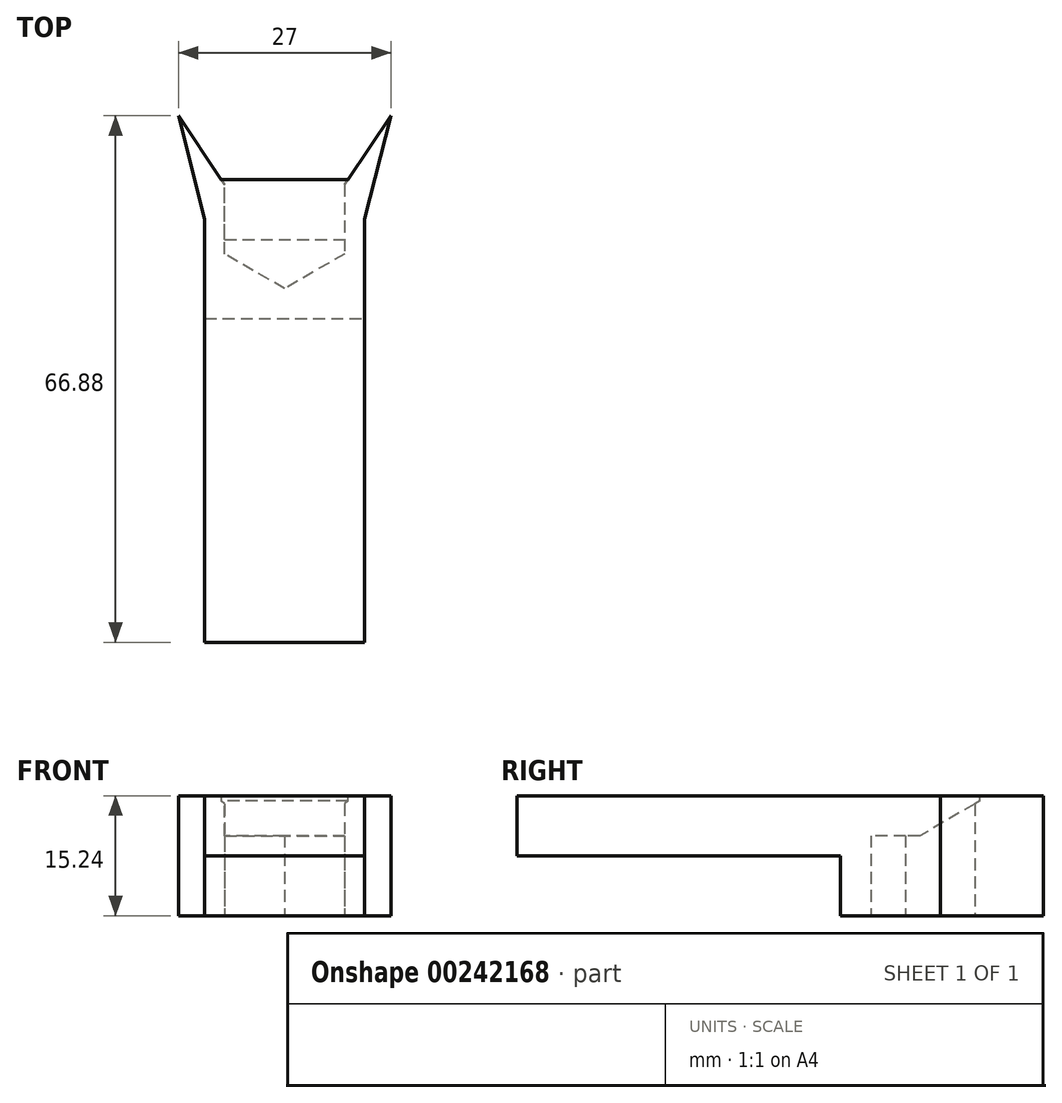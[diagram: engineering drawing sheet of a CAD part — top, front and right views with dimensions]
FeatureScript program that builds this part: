
annotation { "Feature Type Name" : "Feature", "Feature Type Description" : "" }
export const myFeature = defineFeature(function(context is Context, id is Id, definition is map)
    precondition{}
    {
        {
            var Q0;
            Q0=qCreatedBy(makeId("Top.planeOp"),FACE);
            var sketch = newSketch(context, id + "F0", { "sketchPlane" : qUnion([Q0])});
            skLineSegment(sketch, "E0.bottom", {"start": v(-10.19, 14.8) * mm, "end": v(-7.65, 14.8) * mm});
            skLineSegment(sketch, "E0.top", {"start": v(-10.19, -38.95) * mm, "end": v(10.13, -38.95) * mm});
            skLineSegment(sketch, "E0.left", {"start": v(-10.19, 14.8) * mm, "end": v(-10.19, -38.95) * mm});
            skLineSegment(sketch, "E0.right", {"start": v(10.13, 14.8) * mm, "end": v(10.13, -38.95) * mm});
            skArc(sketch, "E1.cCircle", {"start": v(-7.65, 14.8) * mm, "mid": v(-0.03, 7.17) * mm, "end": v(7.6, 14.8) * mm, "construction": true});
            skLineSegment(sketch, "E1.0", {"start": v(7.6, 19.2) * mm, "end": v(7.6, 10.4) * mm});
            skLineSegment(sketch, "E1.1", {"start": v(7.6, 10.4) * mm, "end": v(-0.03, 6) * mm});
            skLineSegment(sketch, "E1.2", {"start": v(-0.03, 6) * mm, "end": v(-7.65, 10.4) * mm});
            skLineSegment(sketch, "E1.3", {"start": v(-7.65, 10.4) * mm, "end": v(-7.65, 19.2) * mm});
            skPoint(sketch, "E1.0.midPoint", {"position": v(7.6, 14.8) * mm});
            skLineSegment(sketch, "E2", {"start": v(-13.5, 27.93) * mm, "end": v(-10.19, 14.8) * mm});
            skLineSegment(sketch, "E3", {"start": v(10.13, 14.8) * mm, "end": v(13.5, 27.93) * mm});
            skLineSegment(sketch, "E4", {"start": v(-13.5, 27.93) * mm, "end": v(-7.65, 19.2) * mm});
            skLineSegment(sketch, "E5", {"start": v(7.6, 19.2) * mm, "end": v(13.5, 27.93) * mm});
            skPoint(sketch, "E6.orphan", {"position": v(-0.03, 23.6) * mm});
            skLineSegment(sketch, "E7.trimOffspring", {"start": v(7.6, 14.8) * mm, "end": v(10.13, 14.8) * mm});
            skSolve(sketch);
        }
        {
            var Q0;
            Q0 = qSketchRegion(id + "F0", true);
            extrude(context, id + "F1", {"entities" : qUnion([Q0]), "depth" : 15.24 * mm});
        }
        {
            var Q0;
            Q0=makeQuery(id+"F1.opExtrude","CAP_FACE",FACE,{"disambiguationData":[OSD([sQuery(id+"F0.wireOp",EDGE,"E0.top"),sQuery(id+"F0.wireOp",EDGE,"E0.left"),sQuery(id+"F0.wireOp",EDGE,"E0.right"),sQuery(id+"F0.wireOp",EDGE,"E1.0"),sQuery(id+"F0.wireOp",EDGE,"E1.1"),sQuery(id+"F0.wireOp",EDGE,"E1.2"),sQuery(id+"F0.wireOp",EDGE,"E1.3"),sQuery(id+"F0.wireOp",EDGE,"E2"),sQuery(id+"F0.wireOp",EDGE,"E3"),sQuery(id+"F0.wireOp",EDGE,"E4"),sQuery(id+"F0.wireOp",EDGE,"E5")])],"isStart":false});
            var sketch = newSketch(context, id + "F2", { "sketchPlane" : qUnion([Q0])});
            skLineSegment(sketch, "E8.bottom", {"start": v(-9.78, 19.84) * mm, "end": v(9.46, 19.84) * mm});
            skLineSegment(sketch, "E8.top", {"start": v(-9.78, 4.74) * mm, "end": v(9.46, 4.74) * mm});
            skLineSegment(sketch, "E8.left", {"start": v(-9.78, 19.84) * mm, "end": v(-9.78, 4.74) * mm});
            skLineSegment(sketch, "E8.right", {"start": v(9.46, 19.84) * mm, "end": v(9.46, 4.74) * mm});
            skSolve(sketch);
        }
        {
            var Q0;
            Q0 = qSketchRegion(id + "F2", true);
            extrude(context, id + "F3", {"entities" : qUnion([Q0]), "operationType" : NewBodyOperationType.ADD, "oppositeDirection" : true, "depth" : 5.08 * mm});
        }
        {
            var Q0;
            Q0=makeQuery(id+"F3.opExtrude","CAP_EDGE",EDGE,{"disambiguationData":[OSD([sQuery(id+"F2.wireOp",EDGE,"E8.bottom")])],"isStart":false});
            chamfer(context, id + "F4", {"entities" : qUnion([Q0]), "chamferType" : ChamferType.OFFSET_ANGLE, "width" : 7.62 * mm, "oppositeDirection" : false, "angle" : 30 * degree, "tangentPropagation" : true});
        }
        {
            var Q0;
            Q0=makeQuery(id+"F1.opExtrude","CAP_FACE",FACE,{"disambiguationData":[OSD([sQuery(id+"F0.wireOp",EDGE,"E0.top"),sQuery(id+"F0.wireOp",EDGE,"E0.left"),sQuery(id+"F0.wireOp",EDGE,"E0.right"),sQuery(id+"F0.wireOp",EDGE,"E1.0"),sQuery(id+"F0.wireOp",EDGE,"E1.1"),sQuery(id+"F0.wireOp",EDGE,"E1.2"),sQuery(id+"F0.wireOp",EDGE,"E1.3"),sQuery(id+"F0.wireOp",EDGE,"E2"),sQuery(id+"F0.wireOp",EDGE,"E3"),sQuery(id+"F0.wireOp",EDGE,"E4"),sQuery(id+"F0.wireOp",EDGE,"E5")])],"isStart":true});
            var sketch = newSketch(context, id + "F5", { "sketchPlane" : qUnion([Q0])});
            skLineSegment(sketch, "E9.bottom", {"start": v(-10.19, -2.14) * mm, "end": v(10.13, -2.14) * mm});
            skLineSegment(sketch, "E9.top", {"start": v(-10.19, 38.95) * mm, "end": v(10.13, 38.95) * mm});
            skLineSegment(sketch, "E9.left", {"start": v(-10.19, -2.14) * mm, "end": v(-10.19, 38.95) * mm});
            skLineSegment(sketch, "E9.right", {"start": v(10.13, -2.14) * mm, "end": v(10.13, 38.95) * mm});
            skSolve(sketch);
        }
        {
            var Q0;
            Q0=makeQuery(id+"F5.imprint","IMPRINT",FACE,{"disambiguationData":[TD([[makeQuery(id+"F5.imprint","IMPRINT",EDGE,{"derivedFrom":sQuery(id+"F5.wireOp",EDGE,"E9.bottom")}),1.0]])]});
            extrude(context, id + "F6", {"entities" : qUnion([Q0]), "operationType" : NewBodyOperationType.REMOVE, "oppositeDirection" : true, "depth" : 7.62 * mm});
        }
    });
